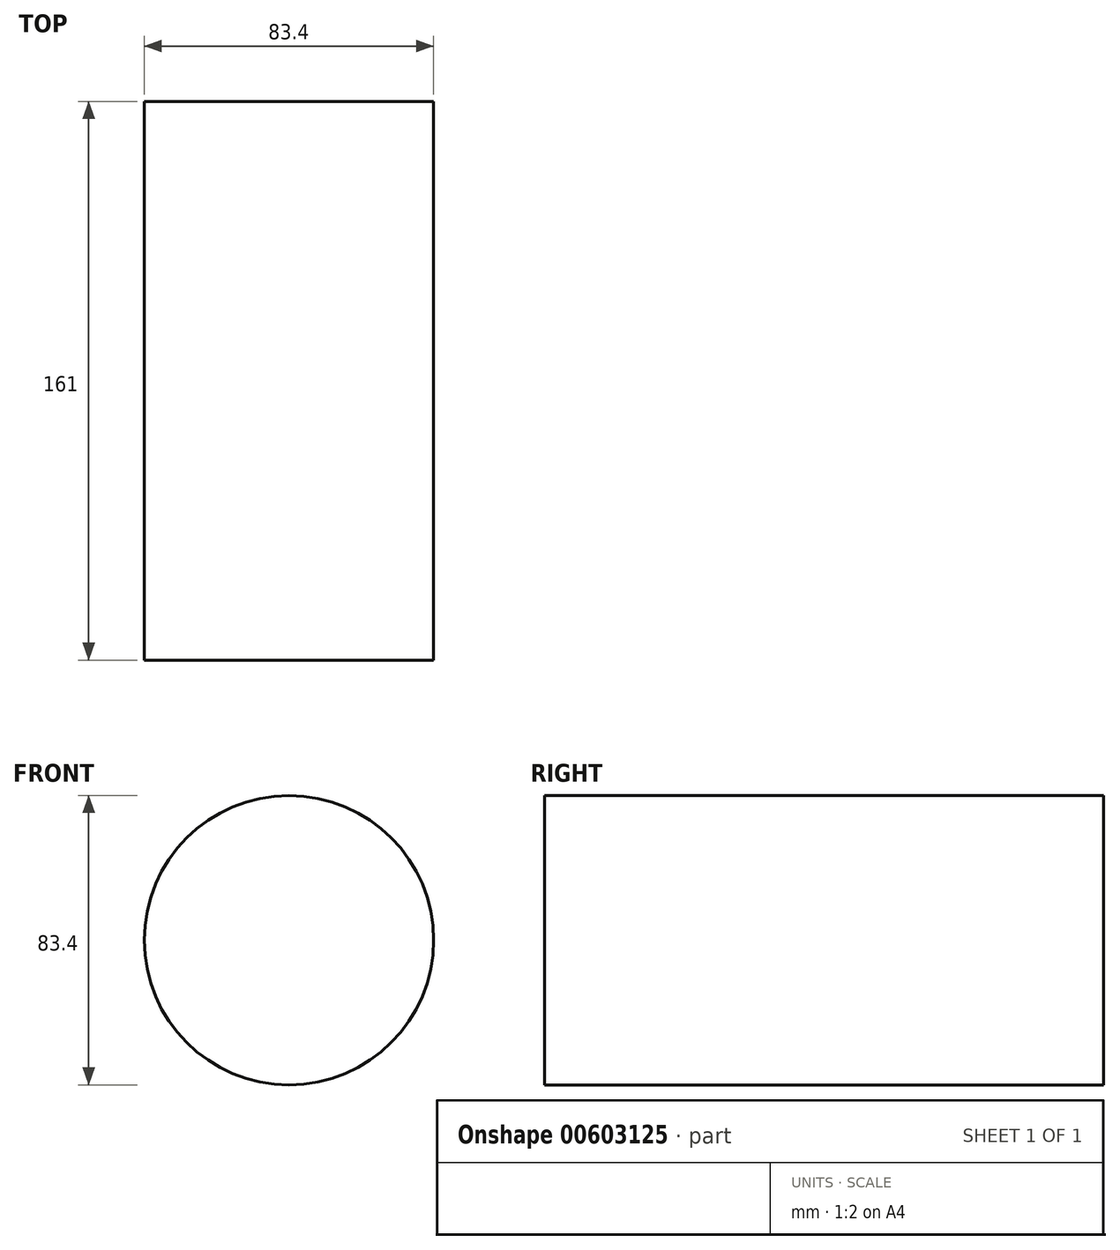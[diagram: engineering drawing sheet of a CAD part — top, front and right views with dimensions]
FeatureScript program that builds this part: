
annotation { "Feature Type Name" : "Feature", "Feature Type Description" : "" }
export const myFeature = defineFeature(function(context is Context, id is Id, definition is map)
    precondition{}
    {
        {
            var Q0;
            Q0=qCreatedBy(makeId("Front.planeOp"),FACE);
            var sketch = newSketch(context, id + "F0", { "sketchPlane" : qUnion([Q0])});
            skCircle(sketch, "E0", {"center": v(0, 0) * mm, "radius": 41.7 * mm});
            skSolve(sketch);
        }
        {
            var Q0;
            Q0 = qSketchRegion(id + "F0", true);
            extrude(context, id + "F1", {"entities" : qUnion([Q0]), "depth" : 161 * mm, "offsetDistance" : 25 * mm});
        }
    });
